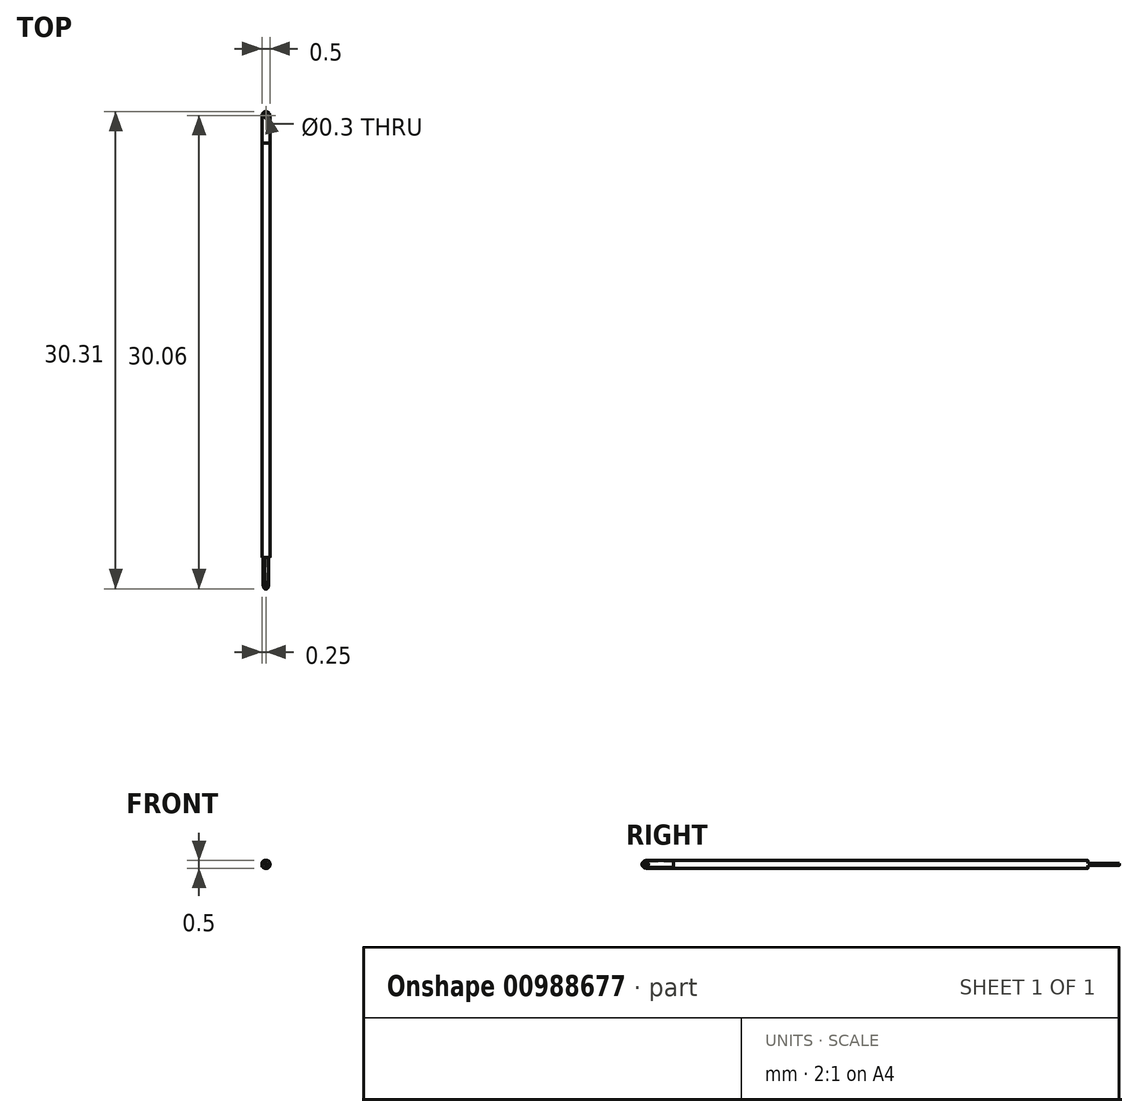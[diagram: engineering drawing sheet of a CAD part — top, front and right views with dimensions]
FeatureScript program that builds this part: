
annotation { "Feature Type Name" : "Feature", "Feature Type Description" : "" }
export const myFeature = defineFeature(function(context is Context, id is Id, definition is map)
    precondition{}
    {
        {
            var Q0;
            Q0=qCreatedBy(makeId("Top.planeOp"),FACE);
            var sketch = newSketch(context, id + "F0", { "sketchPlane" : qUnion([Q0])});
            skCircle(sketch, "E0", {"center": v(0, 0) * mm, "radius": 0.15 * mm});
            skCircle(sketch, "E1", {"center": v(0, 29.8) * mm, "radius": 0.15 * mm});
            skCircle(sketch, "E2", {"center": v(0, 0) * mm, "radius": 0.25 * mm});
            skCircle(sketch, "E3", {"center": v(0, 29.8) * mm, "radius": 0.25 * mm});
            skLineSegment(sketch, "E4", {"start": v(-0.25, 29.8) * mm, "end": v(-0.25, 0) * mm});
            skLineSegment(sketch, "E5", {"start": v(0.25, 0) * mm, "end": v(0.25, 29.8) * mm});
            skLineSegment(sketch, "E6.bottom", {"start": v(-0.25, 0) * mm, "end": v(0.25, 0) * mm});
            skLineSegment(sketch, "E6.top", {"start": v(-0.25, -0.25) * mm, "end": v(0.25, -0.25) * mm});
            skLineSegment(sketch, "E6.left", {"start": v(-0.25, 0) * mm, "end": v(-0.25, -0.25) * mm});
            skLineSegment(sketch, "E6.right", {"start": v(0.25, 0) * mm, "end": v(0.25, -0.25) * mm});
            skLineSegment(sketch, "E7", {"start": v(-0.25, 1.75) * mm, "end": v(0.25, 1.75) * mm});
            skSolve(sketch);
        }
        {
            var Q0;
            {var subQ5=sQuery(id+"F0.wireOp",EDGE,"E7");Q0=makeQuery(id+"F0.imprint","IMPRINT",FACE,{"disambiguationData":[TD([[makeQuery(id+"F0.imprint","IMPRINT",EDGE,{"derivedFrom":subQ5}),1.0]])]});}
            var Q1;
            Q1=makeQuery(id+"F0.imprint","IMPRINT",FACE,{"disambiguationData":[TD([[makeQuery(id+"F0.imprint","IMPRINT",EDGE,{"derivedFrom":sQuery(id+"F0.wireOp",EDGE,"E1")}),-1.0]])]});
            extrude(context, id + "F1", {"entities" : qUnion([Q0, Q1]), "endBound" : BoundingType.SYMMETRIC, "depth" : 0.1 * mm, "offsetDistance" : 25 * mm});
        }
        {
            var Q0;
            Q0=makeQuery(id+"F1.opExtrude","CAP_FACE",FACE,{"disambiguationData":[OSD([sQuery(id+"F0.wireOp",EDGE,"E1"),sQuery(id+"F0.wireOp",EDGE,"E3"),sQuery(id+"F0.wireOp",EDGE,"E4"),sQuery(id+"F0.wireOp",EDGE,"E5"),sQuery(id+"F0.wireOp",EDGE,"E7")])],"isStart":false});
            var sketch = newSketch(context, id + "F2", { "sketchPlane" : qUnion([Q0])});
            skLineSegment(sketch, "E8", {"start": v(-0.25, 28.06) * mm, "end": v(0.25, 28.06) * mm});
            skSolve(sketch);
        }
        {
            var Q0;
            {var subQ0=sQuery(id+"F2.wireOp",EDGE,"E8");Q0=makeQuery(id+"F2.imprint","IMPRINT",FACE,{"disambiguationData":[TD([[makeQuery(id+"F2.imprint","IMPRINT",EDGE,{"derivedFrom":subQ0}),-1.0]])]});}
            extrude(context, id + "F3", {"entities" : qUnion([Q0]), "operationType" : NewBodyOperationType.ADD, "depth" : 0.2 * mm, "offsetDistance" : 25 * mm});
        }
        {
            var Q0;
            Q0=makeQuery(id+"F1.opExtrude","CAP_FACE",FACE,{"disambiguationData":[OSD([sQuery(id+"F0.wireOp",EDGE,"E1"),sQuery(id+"F0.wireOp",EDGE,"E3"),sQuery(id+"F0.wireOp",EDGE,"E4"),sQuery(id+"F0.wireOp",EDGE,"E5"),sQuery(id+"F0.wireOp",EDGE,"E7")])],"isStart":true});
            var sketch = newSketch(context, id + "F4", { "sketchPlane" : qUnion([Q0])});
            skLineSegment(sketch, "E9", {"start": v(0.25, -28.06) * mm, "end": v(-0.25, -28.06) * mm});
            skSolve(sketch);
        }
        {
            var Q0;
            {var subQ0=sQuery(id+"F4.wireOp",EDGE,"E9");Q0=makeQuery(id+"F4.imprint","IMPRINT",FACE,{"disambiguationData":[TD([[makeQuery(id+"F4.imprint","IMPRINT",EDGE,{"derivedFrom":subQ0}),-1.0]])]});}
            extrude(context, id + "F5", {"entities" : qUnion([Q0]), "operationType" : NewBodyOperationType.ADD, "depth" : 0.2 * mm, "offsetDistance" : 25 * mm});
        }
        {
            var Q0;
            {var subQ0=sQuery(id+"F0.wireOp",EDGE,"E7");Q0=makeQuery(id+"F5.boolean.opBoolean","MERGE",FACE,{"derivedFrom":[makeQuery(id+"F3.boolean.opBoolean","MERGE",FACE,{"derivedFrom":[makeQuery(id+"F1.opExtrude","SWEPT_FACE",FACE,{"disambiguationData":[OSD([subQ0])]}),makeQuery(id+"F3.opExtrude","SWEPT_FACE",FACE,{"disambiguationData":[OSD([subQ0])]})]}),makeQuery(id+"F5.opExtrude","SWEPT_FACE",FACE,{"disambiguationData":[OSD([subQ0])]})]});}
            var sketch = newSketch(context, id + "F6", { "sketchPlane" : qUnion([Q0])});
            skLineSegment(sketch, "E10.bottom", {"start": v(-0.25, 0.05) * mm, "end": v(0.25, 0.05) * mm});
            skLineSegment(sketch, "E10.top", {"start": v(-0.25, -0.05) * mm, "end": v(0.25, -0.05) * mm});
            skLineSegment(sketch, "E10.left", {"start": v(-0.25, 0.05) * mm, "end": v(-0.25, -0.05) * mm});
            skLineSegment(sketch, "E10.right", {"start": v(0.25, 0.05) * mm, "end": v(0.25, -0.05) * mm});
            skPoint(sketch, "E10.middle", {"position": v(0, 0) * mm});
            skLineSegment(sketch, "E11", {"start": v(0.25, 0.05) * mm, "end": v(0.25, 0.25) * mm});
            skLineSegment(sketch, "E12", {"start": v(-0.08, 0.24) * mm, "end": v(0.17, -0.2) * mm});
            skLineSegment(sketch, "E13", {"start": v(-0.08, 0.24) * mm, "end": v(-0.17, 0.2) * mm});
            skLineSegment(sketch, "E14", {"start": v(-0.17, 0.2) * mm, "end": v(0.08, -0.24) * mm});
            skLineSegment(sketch, "E15", {"start": v(0.17, -0.2) * mm, "end": v(0.08, -0.24) * mm});
            skSolve(sketch);
        }
        {
            var Q0;
            {var subQ5=sQuery(id+"F6.wireOp",EDGE,"E13");Q0=makeQuery(id+"F6.imprint","IMPRINT",FACE,{"disambiguationData":[TD([[makeQuery(id+"F6.imprint","IMPRINT",EDGE,{"derivedFrom":subQ5}),1.0]])]});}
            var Q1;
            {var subQ0=sQuery(id+"F6.wireOp",EDGE,"E14");var subQ1=sQuery(id+"F6.wireOp",EDGE,"E10.bottom");var subQ2=makeQuery(id+"F6.imprint","INTERSECT",VERTEX,{"derivedFrom":[subQ1,subQ0]});Q1=makeQuery(id+"F6.imprint","IMPRINT",FACE,{"disambiguationData":[TD([[makeQuery(id+"F6.imprint","IMPRINT",EDGE,{"disambiguationData":[TD([[subQ2,-1.0]])],"derivedFrom":subQ1}),-1.0]])]});}
            var Q2;
            {var subQ5=sQuery(id+"F6.wireOp",EDGE,"E15");Q2=makeQuery(id+"F6.imprint","IMPRINT",FACE,{"disambiguationData":[TD([[makeQuery(id+"F6.imprint","IMPRINT",EDGE,{"derivedFrom":subQ5}),-1.0]])]});}
            extrude(context, id + "F7", {"entities" : qUnion([Q0, Q1, Q2]), "operationType" : NewBodyOperationType.ADD, "depth" : 2 * mm, "offsetDistance" : 25 * mm});
        }
        {
            var Q0;
            Q0=makeQuery(id+"F7.opExtrude","SWEPT_FACE",FACE,{"disambiguationData":[OSD([sQuery(id+"F6.wireOp",EDGE,"E12")])]});
            var sketch = newSketch(context, id + "F8", { "sketchPlane" : qUnion([Q0])});
            skCircle(sketch, "E16", {"center": v(0, 0) * mm, "radius": 0.25 * mm});
            skCircle(sketch, "E17", {"center": v(0, 0) * mm, "radius": 0.15 * mm});
            skSolve(sketch);
        }
        {
            var Q0;
            {var subQ0=sQuery(id+"F8.wireOp",EDGE,"E16");var subQ1=sQuery(id+"F6.wireOp",EDGE,"E12");var subQ4=makeQuery(id+"F7.opExtrude","CAP_EDGE",EDGE,{"disambiguationData":[OSD([subQ1])],"isStart":false});var subQ5=makeQuery(id+"F8.imprint","INTERSECT",VERTEX,{"derivedFrom":[subQ4,subQ0]});Q0=makeQuery(id+"F8.imprint","IMPRINT",FACE,{"disambiguationData":[TD([[makeQuery(id+"F8.imprint","IMPRINT",EDGE,{"disambiguationData":[TD([[subQ5,1.0]])],"derivedFrom":subQ0}),-1.0]])]});}
            var Q1;
            {var subQ0=sQuery(id+"F8.wireOp",EDGE,"E16");var subQ1=sQuery(id+"F6.wireOp",EDGE,"E12");var subQ4=makeQuery(id+"F7.opExtrude","CAP_EDGE",EDGE,{"disambiguationData":[OSD([subQ1])],"isStart":false});var subQ5=makeQuery(id+"F8.imprint","INTERSECT",VERTEX,{"derivedFrom":[subQ4,subQ0]});Q1=makeQuery(id+"F8.imprint","IMPRINT",FACE,{"disambiguationData":[TD([[makeQuery(id+"F8.imprint","IMPRINT",EDGE,{"disambiguationData":[TD([[subQ5,-1.0]])],"derivedFrom":subQ0}),-1.0]])]});}
            var Q2;
            Q2=makeQuery(id+"F8.imprint","IMPRINT",FACE,{"disambiguationData":[TD([[makeQuery(id+"F8.imprint","IMPRINT",EDGE,{"derivedFrom":sQuery(id+"F8.wireOp",EDGE,"E17")}),1.0]])]});
            extrude(context, id + "F9", {"entities" : qUnion([Q0, Q1, Q2]), "operationType" : NewBodyOperationType.REMOVE, "oppositeDirection" : true, "depth" : 0.5 * mm, "offsetDistance" : 25 * mm});
        }
        {
            var Q0;
            Q0=makeQuery(id+"F3.opExtrude","CAP_EDGE",EDGE,{"disambiguationData":[OSD([sQuery(id+"F0.wireOp",EDGE,"E5")])],"isStart":false});
            var Q1;
            Q1=makeQuery(id+"F3.opExtrude","CAP_EDGE",EDGE,{"disambiguationData":[OSD([sQuery(id+"F0.wireOp",EDGE,"E4")])],"isStart":false});
            var Q2;
            Q2=makeQuery(id+"F5.opExtrude","CAP_EDGE",EDGE,{"disambiguationData":[OSD([sQuery(id+"F0.wireOp",EDGE,"E5")])],"isStart":false});
            var Q3;
            Q3=makeQuery(id+"F5.opExtrude","CAP_EDGE",EDGE,{"disambiguationData":[OSD([sQuery(id+"F0.wireOp",EDGE,"E4")])],"isStart":false});
            fillet(context, id + "F10", {"entities" : qUnion([Q0, Q1, Q2, Q3]), "radius" : 0.2 * mm, "tangentPropagation" : true, "allowEdgeOverflow" : false});
        }
    });
